# Revit family: 6240_Schweißanschluss flachdichtend
name_source: partatom
category: Rohrformteile
units: mm (PartAtom-declared; Revit-internal decimal feet)

## family parameters
Arbeitsebenenbasiert = Nein
Beim Laden mit Abzugskörper schneiden = Nein
Bemaßung runder Anschluss = Durchmesser verwenden
Gemeinsam genutzt = Nein
Immer vertikal = Ja
OmniClass-Nummer = 23.65.55.14
OmniClass-Titel = Valves for Liquid Services
Teiletyp = Verbindung

## types (6) — shared parameters
Ausführung = Schweißanschluss flachdichtend, Mutter und Dichtung.
Flachdichtung = Klinger SIL- C4400
Hersteller = HERZ Armaturen Ges.m.b.H.
Max. Betriebsdruck = 1000000.0 Pa
Max. Betriebstemperatur = 110 °C
Medium = Heizungswasser nach ÖNORM H5195 oder VDI- Richtlinie 2035.
Die Verwendung von Ethylen- oder Propyleneglykol in einem Mischungsverhältnis 25- 50% ist zulässig.
Mutter = Messing CW614N, vernickelt
S02 = 8 mm  [stored 0.0262467 ft]
SCRNCODE = 07;01;02
SCRNSEQ = AWI;AWI_TYP="1001";2
Schweißanschluss = Stahl 1.0576
URL = www.herz-armaturen.at
zero-valued in all types: Vorgabe-Ansicht

## per-type parameters (varying)
| type | D00 | D01 | D02 | GT | L00 | L01 | Nennweite_IG | Nennweite_Schweiß | S01 |
| G3/4 x 21.3 | 17 mm | 10 mm  [stored 0.0328084 ft] | 11 mm | 10 mm  [stored 0.0328084 ft] | 54 mm  [stored 0.177165 ft] | 14 mm  [stored 0.0459318 ft] | 20 mm  [stored 0.0656168 ft] | 15 mm  [stored 0.0492126 ft] | 10 mm  [stored 0.0328084 ft] |
| G1 x 26.8 | 20 mm  [stored 0.0656168 ft] | 13 mm | 13 mm | 12 mm  [stored 0.0393701 ft] | 56 mm  [stored 0.183727 ft] | 17 mm | 25 mm  [stored 0.082021 ft] | 20 mm  [stored 0.0656168 ft] | 12 mm  [stored 0.0393701 ft] |
| G1 1/4 x 33.7 | 26 mm | 16 mm  [stored 0.0524934 ft] | 17 mm | 10 mm  [stored 0.0328084 ft] | 59 mm | 14 mm  [stored 0.0459318 ft] | 32 mm  [stored 0.104987 ft] | 25 mm  [stored 0.082021 ft] | 10 mm  [stored 0.0328084 ft] |
| G1 1/2 x 41.0 | 30 mm | 20 mm  [stored 0.0656168 ft] | 21 mm | 14 mm  [stored 0.0459318 ft] | 66 mm  [stored 0.216535 ft] | 19 mm  [stored 0.062336 ft] | 40 mm  [stored 0.131234 ft] | 32 mm  [stored 0.104987 ft] | 14 mm  [stored 0.0459318 ft] |
| G1 3/4 x 47.5 | 32 mm  [stored 0.104987 ft] | 20 mm  [stored 0.0656168 ft] | 24 mm | 16 mm  [stored 0.0524934 ft] | 72 mm | 23 mm  [stored 0.0754593 ft] | 40 mm  [stored 0.131234 ft] | 40 mm  [stored 0.131234 ft] | 16 mm  [stored 0.0524934 ft] |
| G2 3/8 x 60.3 | 40 mm  [stored 0.131234 ft] | 25 mm  [stored 0.082021 ft] | 30 mm | 14 mm  [stored 0.0459318 ft] | 74 mm | 23 mm  [stored 0.0754593 ft] | 50 mm  [stored 0.164042 ft] | 50 mm  [stored 0.164042 ft] | 14 mm  [stored 0.0459318 ft] |

note: [stored X ft] marks values corroborated as IEEE doubles in the binary element streams (Revit-internal decimal feet)
